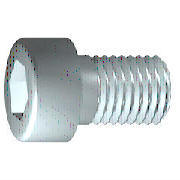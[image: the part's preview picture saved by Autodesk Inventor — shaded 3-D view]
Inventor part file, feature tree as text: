
AUTODESK INVENTOR PART (.ipt)
format: ipt  version: 2015 SP1 (Build 190203100, 203)  size: 187,392 bytes
history: native  units: mm (DEFAULTED — no unit token found)
features: sketch x2, extrude x1, plane x1, fillet x1
ambient origin geometry x7: Origin, YZ Plane, XY Plane, X Axis, Y Axis, Z Axis, Center Point
bodies: Solid1 (feature_tree), Body (feature_tree)
feature tree (5):
  extrude  "Slot"  Depth=3.0mm
  plane  "Work Plane1"
  fillet  "Fillet2"  Radius=3.0mm
  sketch  "Sketch1"  dims[d1=12.0mm d2=0.306825mm d3=3.0mm]
  sketch  "Sketch2"  dims[d4=1.3mm d5=60.0deg d6=3.0mm d7=3.0mm d8=2.886751mm d9=5.5mm d10=90.0deg d11=10.0mm d12=0.0mm d13=12.0mm d14=0.0mm d15=0.306725mm d16=0.306725mm d17=0.3mm d19=0.0mm d26=16.0mm d27=45.0deg d28=0.0mm d29=0.0mm d30=0.1mm]
